# Revit family: 48-SECADOR DE MANOS POTENZA(Recuperación)
name_source: partatom
category: Equipos especializados
revit_build: Autodesk Revit 2018 (Build: 20170223_1515(x64)
units: mm (PartAtom-declared; Revit-internal decimal feet)

## family parameters
Anfitrión = Cara
Compartido = No
Corte con vacíos al cargar = No
Cota de conector redondo = Diámetro de uso
Número OmniClass = 23.45.00.00
Punto de cálculo de habitación = No
Tipo de pieza = Normal
Título OmniClass = Sanitary, Laundry, and Cleaning Equipment

## types (1)
- 48-SECADOR DE MANOS POTENZA(Recuperación)
    Acabado = Brillante
    Altura Nominal = 225
    Ancho Nominal = 174
    Características = Tiempo promedio de secado 40 segundos, apagado automático, rango de sensado de 12-3 cm
    Color = Satinado
    Código de montaje = E1010600
    Descripción = Laundry & Dry Cleanig Equipment
    Descripción IFC = Potenza secador de manos
    Descripción de la garantía = Garantía de 5 años, garantía de 3 años en acabados.
    Duración Garantía Partes = 5
    Duración Garantía Unidad = Años
    Duración unidad = Años
    Elevación por defecto = 0 mm  [stored 0 ft]
    Fabricante = www.corona.com.co
    Forma = Rectangular
    Logitud Nominal = 225
    Material Acabado = Acero Inoxidable Corona
    Material de Fabricación = Acero Inoxidable
    Nombre = Potenza
    Nombre del Fabricante = Corona
    Número Modelo = 706650001
    Requerimientos Accesibilidad = Automático con sensor
    Responsable Garantías Partes = www.corona.com.co
    Tamaño = 225 x 174 x 265
    Tiempo útil = 5
    Tipo de Activo = Fijo
    Tráfico = Institucional

note: [stored X ft] marks values corroborated as IEEE doubles in the binary element streams (Revit-internal decimal feet)

## geometry (parser evidence)
native form markers: Sweep x2
no freeform markers — native parametric forms only
